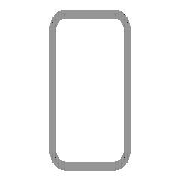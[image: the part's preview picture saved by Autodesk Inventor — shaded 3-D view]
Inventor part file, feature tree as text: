
AUTODESK INVENTOR PART (.ipt)
format: ipt  version: 2025.1 (Build 291241020, 241B)  size: 151,552 bytes
history: native  units: mm (DEFAULTED — no unit token found)
features: other x4, plane x3, split x2, sketch x1
ambient origin geometry x8: Origin, YZ Plane, XZ Plane, XY Plane, X Axis, Y Axis, Z Axis, Center Point
bodies: Solid1 (feature_tree), Body (feature_tree)
feature tree (10):
  parser-record x1  (decoder bookkeeping rows leaked as tree rows — omitted from the tree; the rows remain in map.json)
  other  "Driven Length"
  other  "Start Plane"
  other  "End Plane"
  plane  "Work Plane4"
  split  "Split1"
  plane  "Work Plane5"
  split  "Split2"
  sketch  "Sketch3"  dims[d3=2427.337966mm d4=0.0mm d7=6.0mm d9=40.0mm d11=80.0mm d12=3.0mm d13=-16.666667mm d14=2410.671299mm d15=20.0mm d16=40.0mm d17=90.0deg d18=2427.337966mm]
  plane  "Work Plane3"
